# Revit family: Dock-Shelter_Perma-Tech_Ultra-Dark
name_source: partatom
category: Generic Models
units: mm (PartAtom-declared; Revit-internal decimal feet)

## family parameters
Always vertical = Yes
Can host rebar = No
Cut with Voids When Loaded = Yes
Host = Wall
Maintain Annotation Orientation = No
Part Type = Normal
Room Calculation Point = No
Round Connector Dimension = Use Diameter
Shared = No

## types (1)
- Ultra Dark
    Arcat Spec = https://www.arcat.com
    Bottom Proj. = 6"
    Cost = 0 $
    Cover = Cover Black
    Default Elevation = 0"
    Head Curtain Height = 21"
    Head Curtain Proj. = 9"
    Main Opening = 46"
    Manufacturer = Perma Tech Inc.
    Model = Ultra Dark Soft-Sided Shelter
    Opening Height = 59"
    Opening Width = 26"
    Product Documentation Link = https://www.permatechinc.com
    Product Info = https://www.arcat.com
    Product Page URL = https://www.permatechinc.com
    Rain Dam Proj. = 22"
    Side Curtain Width = 12"
    Side Pad Width = 3"
    Specification = https://www.permatechinc.com
    Top Proj. = 6"
    URL = https://www.permatechinc.com
    Unit Height = 80"
    Unit Width = 50"

## geometry (parser evidence)
native form markers: Sweep x4
no freeform markers — native parametric forms only
